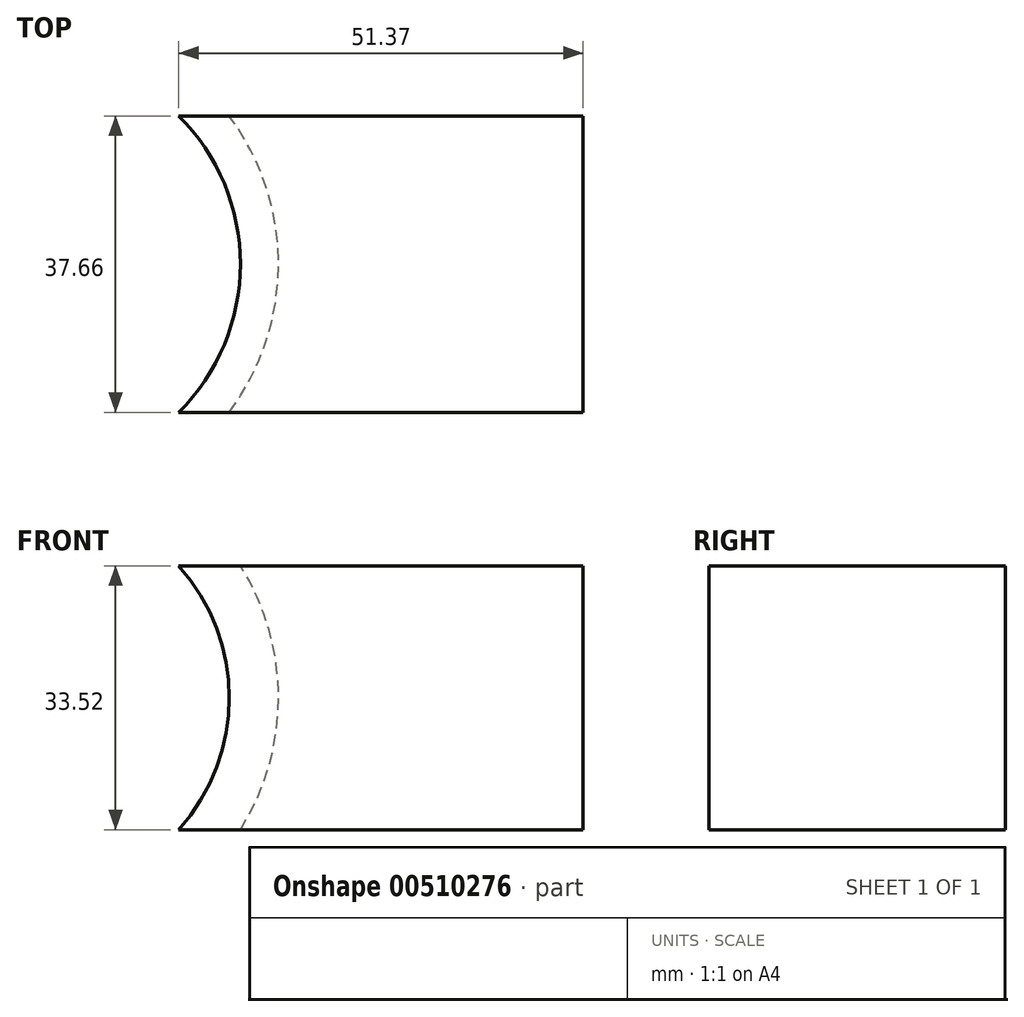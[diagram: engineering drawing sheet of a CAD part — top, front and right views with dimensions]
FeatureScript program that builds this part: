
annotation { "Feature Type Name" : "Feature", "Feature Type Description" : "" }
export const myFeature = defineFeature(function(context is Context, id is Id, definition is map)
    precondition{}
    {
        {
            var Q0;
            Q0=qCreatedBy(makeId("Top.planeOp"),FACE);
            var sketch = newSketch(context, id + "F0", { "sketchPlane" : qUnion([Q0])});
            skArc(sketch, "E0", {"start": v(-75.09, -31.4) * mm, "mid": v(-43.69, 0) * mm, "end": v(-75.09, 31.4) * mm});
            skLineSegment(sketch, "E1", {"start": v(-75.09, -31.4) * mm, "end": v(-75.09, 31.4) * mm, "construction": true});
            skSolve(sketch);
        }
        {
            var Q0;
            Q0=sQuery(id+"F0.wireOp",EDGE,"E0");
            var Q1;
            Q1=sQuery(id+"F0.wireOp",EDGE,"E1");
            revolve(context, id + "F1", {"bodyType" : ToolBodyType.SURFACE, "surfaceEntities" : qUnion([Q0]), "axis" : qUnion([Q1]), "revolveType" : RevolveType.FULL});
        }
        {
            var Q0;
            Q0=qCreatedBy(makeId("Right.planeOp"),FACE);
            var sketch = newSketch(context, id + "F2", { "sketchPlane" : qUnion([Q0])});
            skLineSegment(sketch, "E2.bottom", {"start": v(18.83, 16.76) * mm, "end": v(-18.83, 16.76) * mm});
            skLineSegment(sketch, "E2.top", {"start": v(18.83, -16.76) * mm, "end": v(-18.83, -16.76) * mm});
            skLineSegment(sketch, "E2.left", {"start": v(18.83, 16.76) * mm, "end": v(18.83, -16.76) * mm});
            skLineSegment(sketch, "E2.right", {"start": v(-18.83, 16.76) * mm, "end": v(-18.83, -16.76) * mm});
            skPoint(sketch, "E2.middle", {"position": v(0, 0) * mm});
            skSolve(sketch);
        }
        {
            var Q0;
            Q0=makeQuery(id+"F2.imprint","IMPRINT",FACE,{"disambiguationData":[TD([[makeQuery(id+"F2.imprint","IMPRINT",EDGE,{"derivedFrom":sQuery(id+"F2.wireOp",EDGE,"E2.bottom")}),1.0]])]});
            var Q1;
            Q1=makeQuery(id+"F1.opRevolve","SWEPT_FACE",FACE,{"disambiguationData":[OSD([sQuery(id+"F0.wireOp",EDGE,"E0")])]});
            extrude(context, id + "F3", {"entities" : qUnion([Q0]), "endBound" : BoundingType.UP_TO_NEXT, "oppositeDirection" : true, "depth" : 25 * mm, "endBoundEntityFace" : qUnion([Q1]), "hasOffset" : true, "offsetDistance" : 5 * mm});
        }
    });
